# Revit family: Window-Double_Hung-Pella-Architect_Series-Transom
name_source: partatom
category: Windows
revit_build: Autodesk Revit Architecture 2013 (Build: 20130531_2115(x64)
units: mm (PartAtom-declared; Revit-internal decimal feet)

## types (24) — shared parameters
Analytic Construction = <None>
Architectural Design Manual = To be Determined
Construction Type = -
Cross Grille Pattern = No
Custom Grille Pattern = No
Custom Horizontal Lites = 2
Custom Vertical Lites = 3
Default Sill Height = 2' - 7 1/2"
Description = Double Hung - Transom Unit
Egress Window = No
Energy Efficiency = http://www.pella.com
Environmental Commitment = http://www.pella.com
Ext Finish = Aluminum - Pella - Brown
Glazing Finish = Glass - Pella - Clear Insulating Glass
Glazing Thickness = 0' - 0 5/8"
Grille Visibility = Yes
Heat Transfer Coefficient (U) = 0.1000 BTU/(h·ft²·°F)
Int Finish = Wood - Pella - Pine
Manufacturer = Pella Windows & Doors
Operation = Transom
Prairie Grille Pattern = No
Product Documentation Link = http://media.pella.com
Product Name = Architect Series Double-Hung Window
Product Page URL = http://www.pella.com
Series = Architect Series - Aluminum-Clad Wood
Size Constraints = Window Sizing constraints available in 6.35 mm increments
Thermal Resistance (R) = 10.0000 (h·ft²·°F)/BTU
Top Row Grille Pattern = No
Traditional Grille Pattern = Yes
URL = www.pella.com
Wall Closure = By host
zero-valued in all types: Solar Heat Gain Coefficient, Visual Light Transmittance

## per-type parameters (varying)
| type | Head Height | Height | Rough Height | Rough Width | Sash Height | Sash Width | Unit Height | Unit Width | Width |
| 2114 | 3' - 9 1/2" | 1' - 2" | 1' - 2 3/4" | 1' - 9 3/4" | 0' - 11 1/2" | 1' - 6 1/2" | 1' - 2" | 1' - 9" | 1' - 9" |
| 2117 | 4' - 0 1/2" | 1' - 5" | 1' - 5 3/4" | 1' - 9 3/4" | 1' - 2 1/2" | 1' - 6 1/2" | 1' - 5" | 1' - 9" | 1' - 9" |
| 2125 | 4' - 8 1/2" | 2' - 1" | 2' - 1 3/4" | 1' - 9 3/4" | 1' - 10 1/2" | 1' - 6 1/2" | 2' - 1" | 1' - 9" | 1' - 9" |
| 2514 | 3' - 9 1/2" | 1' - 2" | 1' - 2 3/4" | 2' - 1 3/4" | 0' - 11 1/2" | 1' - 10 1/2" | 1' - 2" | 2' - 1" | 2' - 1" |
| 2517 | 4' - 0 1/2" | 1' - 5" | 1' - 5 3/4" | 2' - 1 3/4" | 1' - 2 1/2" | 1' - 10 1/2" | 1' - 5" | 2' - 1" | 2' - 1" |
| 2525 | 4' - 8 1/2" | 2' - 1" | 2' - 1 3/4" | 2' - 1 3/4" | 1' - 10 1/2" | 1' - 10 1/2" | 2' - 1" | 2' - 1" | 2' - 1" |
| 2914 | 3' - 9 1/2" | 1' - 2" | 1' - 2 3/4" | 2' - 5 3/4" | 0' - 11 1/2" | 2' - 2 1/2" | 1' - 2" | 2' - 5" | 2' - 5" |
| 2917 | 4' - 0 1/2" | 1' - 5" | 1' - 5 3/4" | 2' - 5 3/4" | 1' - 2 1/2" | 2' - 2 1/2" | 1' - 5" | 2' - 5" | 2' - 5" |
| 2925 | 4' - 8 1/2" | 2' - 1" | 2' - 1 3/4" | 2' - 5 3/4" | 1' - 10 1/2" | 2' - 2 1/2" | 2' - 1" | 2' - 5" | 2' - 5" |
| 3314 | 3' - 9 1/2" | 1' - 2" | 1' - 2 3/4" | 2' - 9 3/4" | 0' - 11 1/2" | 2' - 6 1/2" | 1' - 2" | 2' - 9" | 2' - 9" |
| 3317 | 4' - 0 1/2" | 1' - 5" | 1' - 5 3/4" | 2' - 9 3/4" | 1' - 2 1/2" | 2' - 6 1/2" | 1' - 5" | 2' - 9" | 2' - 9" |
| 3325 | 4' - 8 1/2" | 2' - 1" | 2' - 1 3/4" | 2' - 9 3/4" | 1' - 10 1/2" | 2' - 6 1/2" | 2' - 1" | 2' - 9" | 2' - 9" |
| 3714 | 3' - 9 1/2" | 1' - 2" | 1' - 2 3/4" | 3' - 1 3/4" | 0' - 11 1/2" | 2' - 10 1/2" | 1' - 2" | 3' - 1" | 3' - 1" |
| 3717 | 4' - 0 1/2" | 1' - 5" | 1' - 5 3/4" | 3' - 1 3/4" | 1' - 2 1/2" | 2' - 10 1/2" | 1' - 5" | 3' - 1" | 3' - 1" |
| 3725 | 4' - 8 1/2" | 2' - 1" | 2' - 1 3/4" | 3' - 1 3/4" | 1' - 10 1/2" | 2' - 10 1/2" | 2' - 1" | 3' - 1" | 3' - 1" |
| 4114 | 3' - 9 1/2" | 1' - 2" | 1' - 2 3/4" | 3' - 5 3/4" | 0' - 11 1/2" | 3' - 2 1/2" | 1' - 2" | 3' - 5" | 3' - 5" |
| 4117 | 4' - 0 1/2" | 1' - 5" | 1' - 5 3/4" | 3' - 5 3/4" | 1' - 2 1/2" | 3' - 2 1/2" | 1' - 5" | 3' - 5" | 3' - 5" |
| 4125 | 4' - 8 1/2" | 2' - 1" | 2' - 1 3/4" | 3' - 5 3/4" | 1' - 10 1/2" | 3' - 2 1/2" | 2' - 1" | 3' - 5" | 3' - 5" |
| 4514 | 3' - 9 1/2" | 1' - 2" | 1' - 2 3/4" | 3' - 9 3/4" | 0' - 11 1/2" | 3' - 6 1/2" | 1' - 2" | 3' - 9" | 3' - 9" |
| 4517 | 4' - 0 1/2" | 1' - 5" | 1' - 5 3/4" | 3' - 9 3/4" | 1' - 2 1/2" | 3' - 6 1/2" | 1' - 5" | 3' - 9" | 3' - 9" |
| 4525 | 4' - 8 1/2" | 2' - 1" | 2' - 1 3/4" | 3' - 9 3/4" | 1' - 10 1/2" | 3' - 6 1/2" | 2' - 1" | 3' - 9" | 3' - 9" |
| 4814 | 3' - 9 1/2" | 1' - 2" | 1' - 2 3/4" | 4' - 0 3/4" | 0' - 11 1/2" | 3' - 9 1/2" | 1' - 2" | 4' - 0" | 4' - 0" |
| 4817 | 4' - 0 1/2" | 1' - 5" | 1' - 5 3/4" | 4' - 0 3/4" | 1' - 2 1/2" | 3' - 9 1/2" | 1' - 5" | 4' - 0" | 4' - 0" |
| 4825 | 4' - 8 1/2" | 2' - 1" | 2' - 1 3/4" | 4' - 0 3/4" | 1' - 10 1/2" | 3' - 9 1/2" | 2' - 1" | 4' - 0" | 4' - 0" |

note: column(s) folded — value = type name in every type: Model

## geometry (parser evidence)
native form markers: Blend x8, Sweep x6
no freeform markers — native parametric forms only
